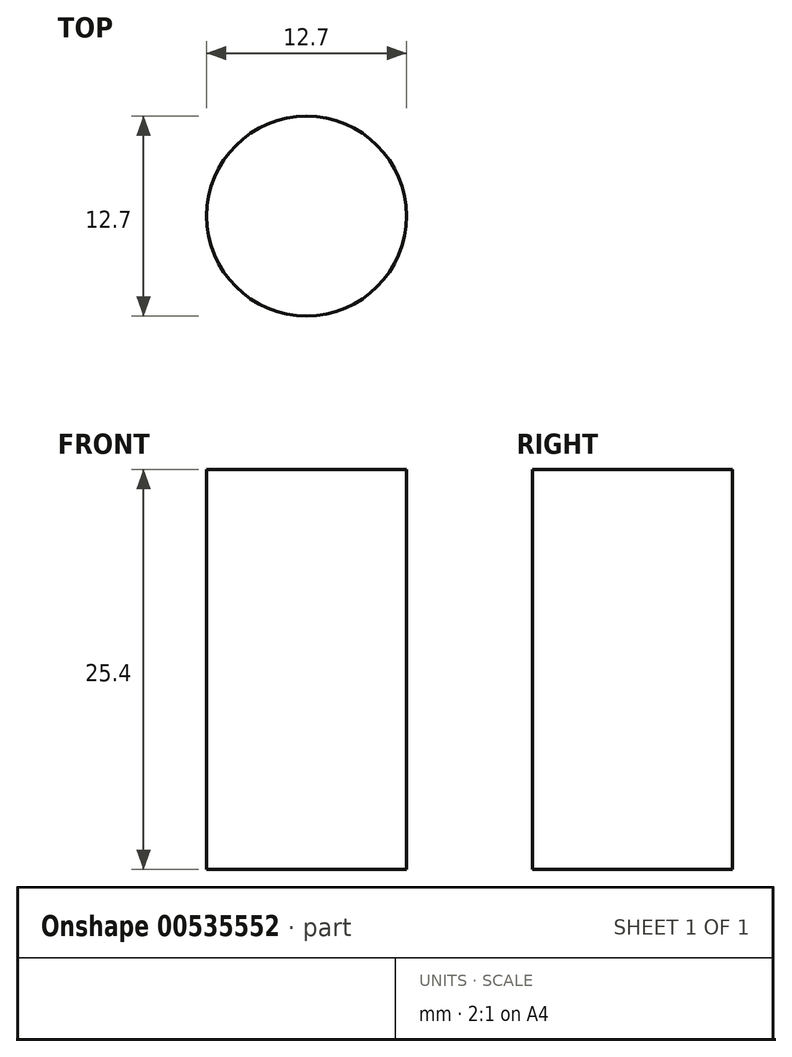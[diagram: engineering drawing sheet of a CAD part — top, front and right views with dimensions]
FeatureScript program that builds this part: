
annotation { "Feature Type Name" : "Feature", "Feature Type Description" : "" }
export const myFeature = defineFeature(function(context is Context, id is Id, definition is map)
    precondition{}
    {
        {
            var Q0;
            Q0=qCreatedBy(makeId("Top.planeOp"),FACE);
            var sketch = newSketch(context, id + "F0", { "sketchPlane" : qUnion([Q0])});
            skCircle(sketch, "E0", {"center": v(0, 0) * mm, "radius": 6.35 * mm});
            skSolve(sketch);
        }
        {
            var Q0;
            Q0 = qSketchRegion(id + "F0", true);
            extrude(context, id + "F1", {"entities" : qUnion([Q0]), "depth" : 25.4 * mm, "offsetDistance" : 25 * mm});
        }
    });
